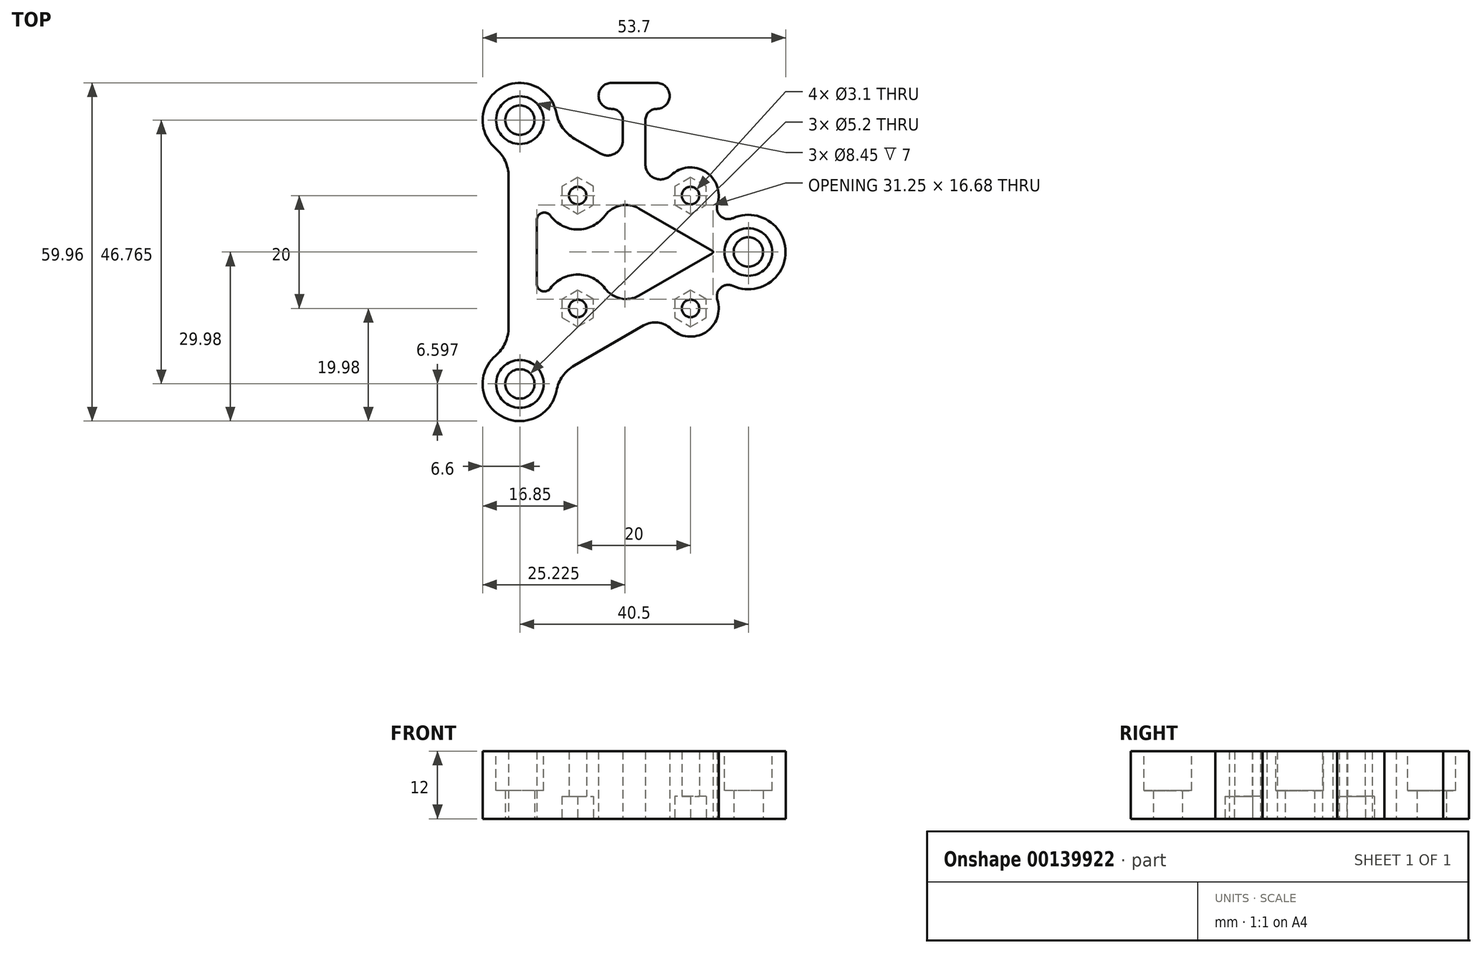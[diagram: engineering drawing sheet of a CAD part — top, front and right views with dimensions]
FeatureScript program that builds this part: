
annotation { "Feature Type Name" : "Feature", "Feature Type Description" : "" }
export const myFeature = defineFeature(function(context is Context, id is Id, definition is map)
    precondition{}
    {
        {
            var Q0;
            Q0=qCreatedBy(makeId("Top.planeOp"),FACE);
            var sketch = newSketch(context, id + "F0", { "sketchPlane" : qUnion([Q0])});
            skLineSegment(sketch, "E0", {"start": v(0, 0) * mm, "end": v(-40.5, -23.38) * mm, "construction": true});
            skLineSegment(sketch, "E1", {"start": v(-40.5, -23.38) * mm, "end": v(-40.5, 23.38) * mm, "construction": true});
            skLineSegment(sketch, "E2", {"start": v(-40.5, 23.38) * mm, "end": v(0, 0) * mm, "construction": true});
            skCircle(sketch, "E3", {"center": v(-40.5, 23.38) * mm, "radius": 2.6 * mm});
            skCircle(sketch, "E4", {"center": v(0, 0) * mm, "radius": 2.6 * mm});
            skCircle(sketch, "E5", {"center": v(-40.5, -23.38) * mm, "radius": 2.6 * mm});
            skLineSegment(sketch, "E6.bottom", {"start": v(-30.25, 10) * mm, "end": v(-10.25, 10) * mm, "construction": true});
            skLineSegment(sketch, "E6.top", {"start": v(-30.25, -10) * mm, "end": v(-10.25, -10) * mm, "construction": true});
            skLineSegment(sketch, "E6.left", {"start": v(-30.25, 10) * mm, "end": v(-30.25, -10) * mm, "construction": true});
            skLineSegment(sketch, "E6.right", {"start": v(-10.25, 10) * mm, "end": v(-10.25, -10) * mm, "construction": true});
            skPoint(sketch, "E7", {"position": v(-30.25, 0) * mm});
            skLineSegment(sketch, "E8", {"start": v(-30.25, 0) * mm, "end": v(-40.5, 0) * mm, "construction": true});
            skPoint(sketch, "E9", {"position": v(-10.25, 0) * mm});
            skLineSegment(sketch, "E10", {"start": v(-10.25, 0) * mm, "end": v(0, 0) * mm, "construction": true});
            skCircle(sketch, "E11", {"center": v(-30.25, 10) * mm, "radius": 1.55 * mm});
            skCircle(sketch, "E12", {"center": v(-10.25, 10) * mm, "radius": 1.55 * mm});
            skCircle(sketch, "E13", {"center": v(-30.25, -10) * mm, "radius": 1.55 * mm});
            skCircle(sketch, "E14", {"center": v(-10.25, -10) * mm, "radius": 1.55 * mm});
            skArc(sketch, "E15", {"start": v(-34.01, 24.6) * mm, "mid": v(-43.8, 29.1) * mm, "end": v(-44.8, 18.38) * mm});
            skArc(sketch, "E16", {"start": v(-44.8, -18.38) * mm, "mid": v(-43.8, -29.1) * mm, "end": v(-34.01, -24.6) * mm});
            skCircle(sketch, "E17", {"center": v(-40.5, 23.38) * mm, "radius": 4.25 * mm, "construction": true});
            skCircle(sketch, "E18", {"center": v(-40.5, -23.38) * mm, "radius": 4.25 * mm, "construction": true});
            skCircle(sketch, "E19", {"center": v(0, 0) * mm, "radius": 4.25 * mm, "construction": true});
            skArc(sketch, "E20", {"start": v(-44.8, -18.38) * mm, "mid": v(-43.1, -16.12) * mm, "end": v(-42.5, -13.37) * mm});
            skArc(sketch, "E21", {"start": v(-34.01, 24.6) * mm, "mid": v(-32.91, 22) * mm, "end": v(-30.83, 20.1) * mm});
            skLineSegment(sketch, "E22", {"start": v(-30.83, -20.1) * mm, "end": v(-18.56, -13.03) * mm});
            skArc(sketch, "E23", {"start": v(-30.83, -20.1) * mm, "mid": v(-32.91, -22) * mm, "end": v(-34.01, -24.6) * mm});
            skLineSegment(sketch, "E24", {"start": v(-22.25, 23.38) * mm, "end": v(-22.25, 19.8) * mm});
            skLineSegment(sketch, "E25", {"start": v(-18.25, 23.38) * mm, "end": v(-18.25, 15.55) * mm});
            skLineSegment(sketch, "E26", {"start": v(-20.25, 29.98) * mm, "end": v(-20.25, 10) * mm, "construction": true});
            skArc(sketch, "E27", {"start": v(-13.7, -13.61) * mm, "mid": v(-16.04, -12.5) * mm, "end": v(-18.56, -13.03) * mm});
            skCircle(sketch, "E28", {"center": v(-10.25, -10) * mm, "radius": 3 * mm, "construction": true});
            skCircle(sketch, "E29", {"center": v(-10.25, 10) * mm, "radius": 3 * mm, "construction": true});
            skCircle(sketch, "E30", {"center": v(-30.25, 10) * mm, "radius": 3 * mm, "construction": true});
            skCircle(sketch, "E31", {"center": v(-30.25, -10) * mm, "radius": 3 * mm, "construction": true});
            skArc(sketch, "E32", {"start": v(-2.72, -6.01) * mm, "mid": v(6.6, 0) * mm, "end": v(-2.72, 6.01) * mm});
            skArc(sketch, "E33", {"start": v(-13.7, -13.61) * mm, "mid": v(-7.6, -14.24) * mm, "end": v(-5.49, -8.48) * mm});
            skArc(sketch, "E34", {"start": v(-5.49, 8.48) * mm, "mid": v(-7.6, 14.24) * mm, "end": v(-13.7, 13.61) * mm});
            skLineSegment(sketch, "E35", {"start": v(0, 0) * mm, "end": v(-10.25, 0) * mm, "construction": true});
            skArc(sketch, "E36", {"start": v(-5.49, 8.48) * mm, "mid": v(-4.9, 6.35) * mm, "end": v(-2.72, 6.01) * mm});
            skArc(sketch, "E37", {"start": v(-2.72, -6.01) * mm, "mid": v(-4.9, -6.35) * mm, "end": v(-5.49, -8.48) * mm});
            skArc(sketch, "E38", {"start": v(-18.25, 15.55) * mm, "mid": v(-16.62, 13.08) * mm, "end": v(-13.7, 13.61) * mm});
            skLineSegment(sketch, "E39", {"start": v(-19.38, 7.72) * mm, "end": v(-6.37, 0.22) * mm});
            skLineSegment(sketch, "E40", {"start": v(-6.37, -0.22) * mm, "end": v(-19.38, -7.72) * mm});
            skArc(sketch, "E41", {"start": v(-6.38, -0.22) * mm, "mid": v(-6.25, 0) * mm, "end": v(-6.38, 0.22) * mm});
            skLineSegment(sketch, "E42", {"start": v(-37.5, 5.67) * mm, "end": v(-37.5, -5.67) * mm});
            skArc(sketch, "E43", {"start": v(-35.1, 6.45) * mm, "mid": v(-30.25, 4) * mm, "end": v(-25.4, 6.45) * mm});
            skArc(sketch, "E44", {"start": v(-25.4, -6.45) * mm, "mid": v(-30.25, -4) * mm, "end": v(-35.1, -6.45) * mm});
            skArc(sketch, "E45", {"start": v(-37.5, -5.67) * mm, "mid": v(-36.58, -6.93) * mm, "end": v(-35.1, -6.45) * mm});
            skArc(sketch, "E46", {"start": v(-35.1, 6.45) * mm, "mid": v(-36.58, 6.93) * mm, "end": v(-37.5, 5.67) * mm});
            skArc(sketch, "E47", {"start": v(-19.38, 7.72) * mm, "mid": v(-22.64, 8.24) * mm, "end": v(-25.4, 6.45) * mm});
            skArc(sketch, "E48", {"start": v(-25.4, -6.45) * mm, "mid": v(-22.64, -8.24) * mm, "end": v(-19.38, -7.72) * mm});
            skLineSegment(sketch, "E49", {"start": v(-30.83, 20.1) * mm, "end": v(-26.28, 17.48) * mm});
            skArc(sketch, "E50", {"start": v(-16.25, 25.38) * mm, "mid": v(-17.66, 24.8) * mm, "end": v(-18.25, 23.38) * mm});
            skArc(sketch, "E51", {"start": v(-24.25, 29.98) * mm, "mid": v(-26.55, 27.68) * mm, "end": v(-24.25, 25.38) * mm});
            skArc(sketch, "E52", {"start": v(-16.25, 25.38) * mm, "mid": v(-13.95, 27.68) * mm, "end": v(-16.25, 29.98) * mm});
            skLineSegment(sketch, "E53", {"start": v(-24.25, 29.98) * mm, "end": v(-16.25, 29.98) * mm});
            skArc(sketch, "E54", {"start": v(-26.28, 17.48) * mm, "mid": v(-23.6, 17.48) * mm, "end": v(-22.25, 19.8) * mm});
            skArc(sketch, "E55", {"start": v(-22.25, 23.38) * mm, "mid": v(-22.84, 24.8) * mm, "end": v(-24.25, 25.38) * mm});
            skLineSegment(sketch, "E56", {"start": v(-22.25, 23.38) * mm, "end": v(-20.25, 23.38) * mm, "construction": true});
            skLineSegment(sketch, "E57", {"start": v(-18.25, 23.38) * mm, "end": v(-20.25, 23.38) * mm, "construction": true});
            skLineSegment(sketch, "E58", {"start": v(-30.25, 10) * mm, "end": v(-40.5, 10) * mm, "construction": true});
            skLineSegment(sketch, "E59", {"start": v(-30.25, -10) * mm, "end": v(-40.5, -10) * mm, "construction": true});
            skLineSegment(sketch, "E60.bottom", {"start": v(-33.75, 21) * mm, "end": v(-6.75, 21) * mm, "construction": true});
            skLineSegment(sketch, "E60.top", {"start": v(-33.75, -21) * mm, "end": v(-6.75, -21) * mm, "construction": true});
            skLineSegment(sketch, "E60.left", {"start": v(-33.75, 21) * mm, "end": v(-33.75, -21) * mm, "construction": true});
            skLineSegment(sketch, "E60.right", {"start": v(-6.75, 21) * mm, "end": v(-6.75, -21) * mm, "construction": true});
            skPoint(sketch, "E61", {"position": v(-20.25, 21) * mm});
            skPoint(sketch, "E62", {"position": v(-6.75, 0) * mm});
            skLineSegment(sketch, "E63", {"start": v(-42.5, -13.37) * mm, "end": v(-42.5, 13.37) * mm});
            skArc(sketch, "E64", {"start": v(-42.5, 13.37) * mm, "mid": v(-43.1, 16.12) * mm, "end": v(-44.8, 18.38) * mm});
            skSolve(sketch);
        }
        {
            var Q0;
            Q0 = qSketchRegion(id + "F0", true);
            extrude(context, id + "F1", {"entities" : qUnion([Q0]), "depth" : 12 * mm, "offsetDistance" : 25 * mm});
        }
        {
            var Q0;
            Q0=makeQuery(id+"F1.opExtrude","CAP_FACE",FACE,{"disambiguationData":[OSD([sQuery(id+"F0.wireOp",EDGE,"E3"),sQuery(id+"F0.wireOp",EDGE,"E4"),sQuery(id+"F0.wireOp",EDGE,"E5"),sQuery(id+"F0.wireOp",EDGE,"E11"),sQuery(id+"F0.wireOp",EDGE,"E12"),sQuery(id+"F0.wireOp",EDGE,"E13"),sQuery(id+"F0.wireOp",EDGE,"E14"),sQuery(id+"F0.wireOp",EDGE,"E15"),sQuery(id+"F0.wireOp",EDGE,"E16"),sQuery(id+"F0.wireOp",EDGE,"j19FQPsl-qwig-UQ58-Jv2b-F3CX3lMaNlr3"),sQuery(id+"F0.wireOp",EDGE,"gmJsRxnh-RUjk-nMxF-1j2H-DpJzBx2kIt6i"),sQuery(id+"F0.wireOp",EDGE,"E20"),sQuery(id+"F0.wireOp",EDGE,"E21"),sQuery(id+"F0.wireOp",EDGE,"E22"),sQuery(id+"F0.wireOp",EDGE,"E23"),sQuery(id+"F0.wireOp",EDGE,"E24"),sQuery(id+"F0.wireOp",EDGE,"ZVHUPO9x-PXRh-jmZE-nEEu-sL8umMgbLI6Z"),sQuery(id+"F0.wireOp",EDGE,"E25"),sQuery(id+"F0.wireOp",EDGE,"FVuNbV8j-3eSL-nEVG-BP8U-f8Nrjsb9kGAF"),sQuery(id+"F0.wireOp",EDGE,"E27"),sQuery(id+"F0.wireOp",EDGE,"E32"),sQuery(id+"F0.wireOp",EDGE,"E33"),sQuery(id+"F0.wireOp",EDGE,"E34"),sQuery(id+"F0.wireOp",EDGE,"E36"),sQuery(id+"F0.wireOp",EDGE,"CuLYsb9Z-ooFL-8SbT-iljd-jO4XptIKYEC7"),sQuery(id+"F0.wireOp",EDGE,"E37")])],"isStart":false});
            var sketch = newSketch(context, id + "F2", { "sketchPlane" : qUnion([Q0])});
            skCircle(sketch, "E65", {"center": v(-40.5, 23.38) * mm, "radius": 4.22 * mm});
            skCircle(sketch, "E66", {"center": v(0, 0) * mm, "radius": 4.22 * mm});
            skCircle(sketch, "E67", {"center": v(-40.5, -23.38) * mm, "radius": 4.22 * mm});
            skSolve(sketch);
        }
        {
            var Q0;
            Q0 = qSketchRegion(id + "F2", true);
            extrude(context, id + "F3", {"entities" : qUnion([Q0]), "operationType" : NewBodyOperationType.REMOVE, "oppositeDirection" : true, "depth" : 7 * mm, "offsetDistance" : 25 * mm});
        }
        {
            var Q0;
            Q0=makeQuery(id+"F1.opExtrude","CAP_FACE",FACE,{"disambiguationData":[OSD([sQuery(id+"F0.wireOp",EDGE,"E3"),sQuery(id+"F0.wireOp",EDGE,"E4"),sQuery(id+"F0.wireOp",EDGE,"E5"),sQuery(id+"F0.wireOp",EDGE,"E11"),sQuery(id+"F0.wireOp",EDGE,"E12"),sQuery(id+"F0.wireOp",EDGE,"E13"),sQuery(id+"F0.wireOp",EDGE,"E14"),sQuery(id+"F0.wireOp",EDGE,"E15"),sQuery(id+"F0.wireOp",EDGE,"E16"),sQuery(id+"F0.wireOp",EDGE,"j19FQPsl-qwig-UQ58-Jv2b-F3CX3lMaNlr3"),sQuery(id+"F0.wireOp",EDGE,"gmJsRxnh-RUjk-nMxF-1j2H-DpJzBx2kIt6i"),sQuery(id+"F0.wireOp",EDGE,"E20"),sQuery(id+"F0.wireOp",EDGE,"E21"),sQuery(id+"F0.wireOp",EDGE,"E22"),sQuery(id+"F0.wireOp",EDGE,"E23"),sQuery(id+"F0.wireOp",EDGE,"E24"),sQuery(id+"F0.wireOp",EDGE,"ZVHUPO9x-PXRh-jmZE-nEEu-sL8umMgbLI6Z"),sQuery(id+"F0.wireOp",EDGE,"E25"),sQuery(id+"F0.wireOp",EDGE,"FVuNbV8j-3eSL-nEVG-BP8U-f8Nrjsb9kGAF"),sQuery(id+"F0.wireOp",EDGE,"E27"),sQuery(id+"F0.wireOp",EDGE,"E32"),sQuery(id+"F0.wireOp",EDGE,"E33"),sQuery(id+"F0.wireOp",EDGE,"E34"),sQuery(id+"F0.wireOp",EDGE,"E36"),sQuery(id+"F0.wireOp",EDGE,"CuLYsb9Z-ooFL-8SbT-iljd-jO4XptIKYEC7"),sQuery(id+"F0.wireOp",EDGE,"E37")])],"isStart":true});
            var sketch = newSketch(context, id + "F4", { "sketchPlane" : qUnion([Q0])});
            skCircle(sketch, "E68.cCircle", {"center": v(-30.25, 10) * mm, "radius": 2.8 * mm, "construction": true});
            skLineSegment(sketch, "E68.0", {"start": v(-27.45, 11.62) * mm, "end": v(-27.45, 8.38) * mm});
            skLineSegment(sketch, "E68.1", {"start": v(-27.45, 8.38) * mm, "end": v(-30.25, 6.77) * mm});
            skLineSegment(sketch, "E68.2", {"start": v(-30.25, 6.77) * mm, "end": v(-33.05, 8.38) * mm});
            skLineSegment(sketch, "E68.3", {"start": v(-33.05, 8.38) * mm, "end": v(-33.05, 11.62) * mm});
            skLineSegment(sketch, "E68.4", {"start": v(-33.05, 11.62) * mm, "end": v(-30.25, 13.23) * mm});
            skLineSegment(sketch, "E68.5", {"start": v(-30.25, 13.23) * mm, "end": v(-27.45, 11.62) * mm});
            skPoint(sketch, "E68.0.midPoint", {"position": v(-27.45, 10) * mm});
            skCircle(sketch, "E69.cCircle", {"center": v(-30.25, -10) * mm, "radius": 2.8 * mm, "construction": true});
            skLineSegment(sketch, "E69.0", {"start": v(-27.45, -8.38) * mm, "end": v(-27.45, -11.62) * mm});
            skLineSegment(sketch, "E69.1", {"start": v(-27.45, -11.62) * mm, "end": v(-30.25, -13.23) * mm});
            skLineSegment(sketch, "E69.2", {"start": v(-30.25, -13.23) * mm, "end": v(-33.05, -11.62) * mm});
            skLineSegment(sketch, "E69.3", {"start": v(-33.05, -11.62) * mm, "end": v(-33.05, -8.38) * mm});
            skLineSegment(sketch, "E69.4", {"start": v(-33.05, -8.38) * mm, "end": v(-30.25, -6.77) * mm});
            skLineSegment(sketch, "E69.5", {"start": v(-30.25, -6.77) * mm, "end": v(-27.45, -8.38) * mm});
            skPoint(sketch, "E69.0.midPoint", {"position": v(-27.45, -10) * mm});
            skCircle(sketch, "E70.cCircle", {"center": v(-10.25, -10) * mm, "radius": 2.8 * mm, "construction": true});
            skLineSegment(sketch, "E70.0", {"start": v(-13.05, -11.62) * mm, "end": v(-13.05, -8.38) * mm});
            skLineSegment(sketch, "E70.1", {"start": v(-13.05, -8.38) * mm, "end": v(-10.25, -6.77) * mm});
            skLineSegment(sketch, "E70.2", {"start": v(-10.25, -6.77) * mm, "end": v(-7.45, -8.38) * mm});
            skLineSegment(sketch, "E70.3", {"start": v(-7.45, -8.38) * mm, "end": v(-7.45, -11.62) * mm});
            skLineSegment(sketch, "E70.4", {"start": v(-7.45, -11.62) * mm, "end": v(-10.25, -13.23) * mm});
            skLineSegment(sketch, "E70.5", {"start": v(-10.25, -13.23) * mm, "end": v(-13.05, -11.62) * mm});
            skPoint(sketch, "E70.0.midPoint", {"position": v(-13.05, -10) * mm});
            skCircle(sketch, "E71.cCircle", {"center": v(-10.25, 10) * mm, "radius": 2.8 * mm, "construction": true});
            skLineSegment(sketch, "E71.0", {"start": v(-13.05, 8.38) * mm, "end": v(-13.05, 11.62) * mm});
            skLineSegment(sketch, "E71.1", {"start": v(-13.05, 11.62) * mm, "end": v(-10.25, 13.23) * mm});
            skLineSegment(sketch, "E71.2", {"start": v(-10.25, 13.23) * mm, "end": v(-7.45, 11.62) * mm});
            skLineSegment(sketch, "E71.3", {"start": v(-7.45, 11.62) * mm, "end": v(-7.45, 8.38) * mm});
            skLineSegment(sketch, "E71.4", {"start": v(-7.45, 8.38) * mm, "end": v(-10.25, 6.77) * mm});
            skLineSegment(sketch, "E71.5", {"start": v(-10.25, 6.77) * mm, "end": v(-13.05, 8.38) * mm});
            skPoint(sketch, "E71.0.midPoint", {"position": v(-13.05, 10) * mm});
            skSolve(sketch);
        }
        {
            var Q0;
            Q0 = qSketchRegion(id + "F4", true);
            extrude(context, id + "F5", {"entities" : qUnion([Q0]), "operationType" : NewBodyOperationType.REMOVE, "oppositeDirection" : true, "depth" : 4 * mm});
        }
    });
